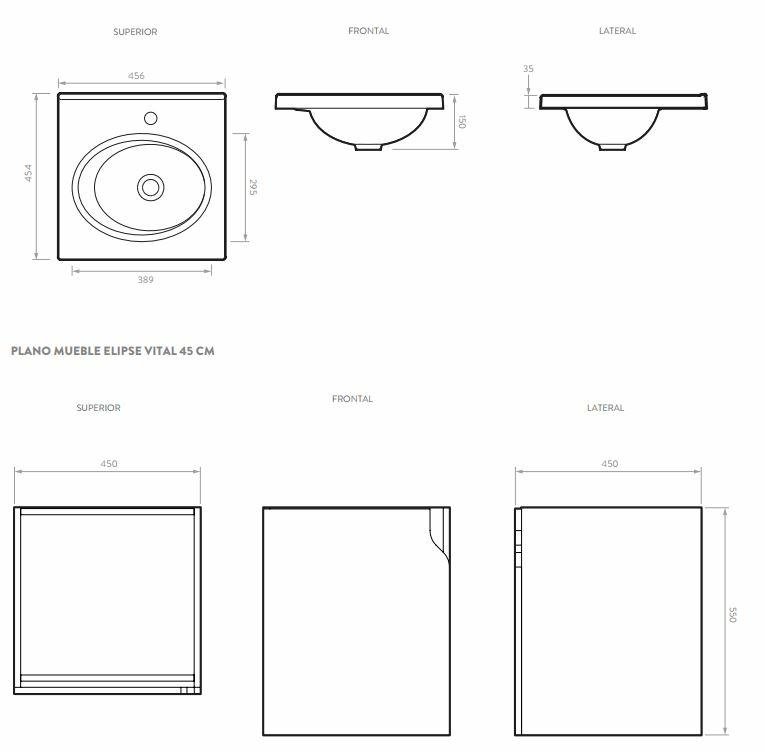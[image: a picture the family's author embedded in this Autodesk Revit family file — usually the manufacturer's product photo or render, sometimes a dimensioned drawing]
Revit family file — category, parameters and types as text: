
# Revit family: LM0046611_Mueble Elipse Vital 80 cm con Lavamanos
name_source: partatom
category: Plumbing Fixtures
units: mm (PartAtom-declared; Revit-internal decimal feet)

## family parameters
Always vertical = Yes
Cut with Voids When Loaded = No
OmniClass Number = 23.45.05.14.14
OmniClass Title = Sinks/Lavatories
Part Type = Normal
Room Calculation Point = No
Round Connector Dimension = Use Diameter
Shared = No
Work Plane-Based = No

## types (2) — shared parameters
Ancho = 606 mm
Description = La línea de muebles Elipse Vital compacto que se se adapta a la gran
mayoría de espacios disponibles
diseño y funcionalidad, ALUVIA se inspira en el movimiento y caída del agua en la
naturaleza, es por ello de sus formas orgánicas donde podemos obtener un producto
compacto y de líneas fluidas, que se adapta en espacios pequeños.
el pricipal benefico de los muebles de esta linea es ser un producto compacto que cuenta
con cajón y repisa brindándole al consumidor mayor capacidad de almacenamiento, como
una excelente solución para aquellos espacios pequeños.
Dimensiones Generales (H * W * P) = 21,65” x 31,50” x 17,72” (550,0 x 800 x 450 mm)
Garantia Madera = 5 años
Manufacturer = Corona
Material Lavamanos = Corona_Cerámica_Sinterizada
Peso Bruto aprox = 36,4 lb (16,5 kg)
Peso Neto aprox = 34,2 lb (15,5 kg)
Profundidad = 435 mm
Referencia = LM0046611
Resistencia a la humedad = 8%
Resistencia al rayado = 700 ciclos

## per-type parameters (varying)
| type | Alto | Canto | Carga máxima | Densidad | Garantia Herrajes | Material | Model | URL |
| Ref. 604281711 Mueble Aluvia Miel Con Lavamanos | 800 mm  [stored 2.62467 ft] |  |  |  |  | Corona_Madera_Carbon |  | https://corona.co |
| Ref. 604286091 Mueble Aluvia Habano Con Lavamanos | 850 mm  [stored 2.78871 ft] | PVC rígido 2 mm de calibre. | 99,2 lb (45 kg). | 15 mms 670 kg./m^3. | 1 año | <By Category> | Mueble aluvia miel LVM 45X45 |  |

note: [stored X ft] marks values corroborated as IEEE doubles in the binary element streams (Revit-internal decimal feet)

## geometry (parser evidence)
native form markers: Sweep x27
no freeform markers — native parametric forms only
